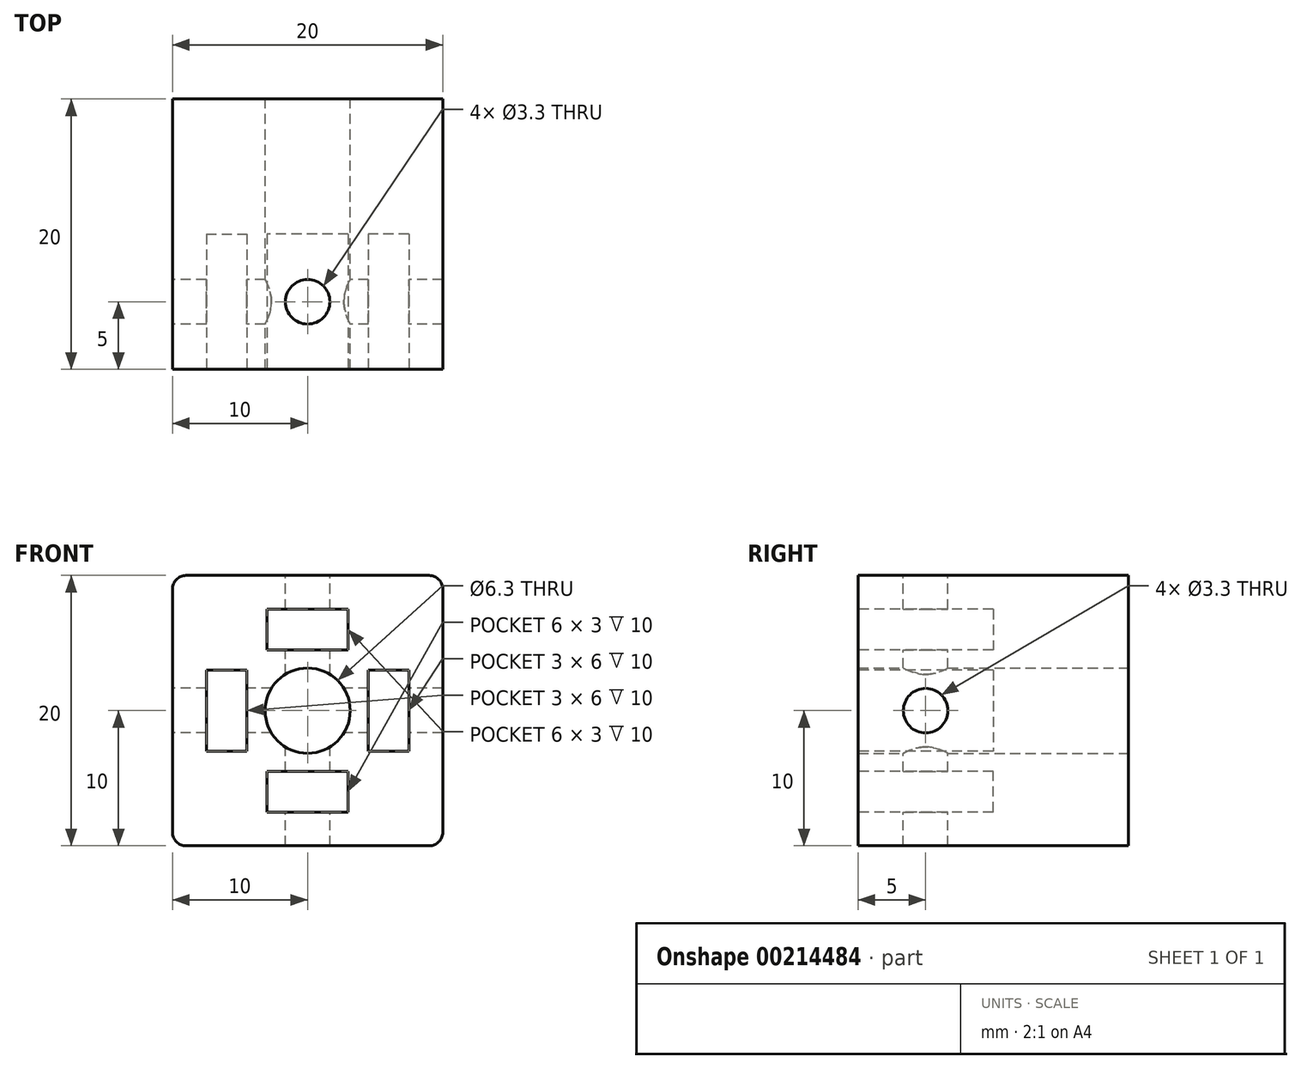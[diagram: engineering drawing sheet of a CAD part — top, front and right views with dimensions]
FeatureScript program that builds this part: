
annotation { "Feature Type Name" : "Feature", "Feature Type Description" : "" }
export const myFeature = defineFeature(function(context is Context, id is Id, definition is map)
    precondition{}
    {
        {
            var Q0;
            Q0=qCreatedBy(makeId("Front.planeOp"),FACE);
            var sketch = newSketch(context, id + "F0", { "sketchPlane" : qUnion([Q0])});
            skLineSegment(sketch, "E0.bottom", {"start": v(10, 10) * mm, "end": v(-10, 10) * mm});
            skLineSegment(sketch, "E0.top", {"start": v(10, -10) * mm, "end": v(-10, -10) * mm});
            skLineSegment(sketch, "E0.left", {"start": v(10, 10) * mm, "end": v(10, -10) * mm});
            skLineSegment(sketch, "E0.right", {"start": v(-10, 10) * mm, "end": v(-10, -10) * mm});
            skPoint(sketch, "E0.middle", {"position": v(0, 0) * mm});
            skCircle(sketch, "E1", {"center": v(0, 0) * mm, "radius": 3.15 * mm});
            skSolve(sketch);
        }
        {
            var Q0;
            Q0 = qSketchRegion(id + "F0", true);
            extrude(context, id + "F1", {"entities" : qUnion([Q0]), "depth" : 20 * mm});
        }
        {
            var Q0;
            Q0=makeQuery(id+"F1.opExtrude","CAP_FACE",FACE,{"disambiguationData":[OSD([sQuery(id+"F0.wireOp",EDGE,"E0.bottom"),sQuery(id+"F0.wireOp",EDGE,"E0.top"),sQuery(id+"F0.wireOp",EDGE,"E0.left"),sQuery(id+"F0.wireOp",EDGE,"E0.right"),sQuery(id+"F0.wireOp",EDGE,"E1")])],"isStart":false});
            var sketch = newSketch(context, id + "F2", { "sketchPlane" : qUnion([Q0])});
            skLineSegment(sketch, "E2", {"start": v(0, 10) * mm, "end": v(0, -10) * mm, "construction": true});
            skLineSegment(sketch, "E3", {"start": v(-10, 0) * mm, "end": v(10, 0) * mm, "construction": true});
            skLineSegment(sketch, "E4.bottom", {"start": v(3, 7.5) * mm, "end": v(-3, 7.5) * mm});
            skLineSegment(sketch, "E4.top", {"start": v(3, 4.5) * mm, "end": v(-3, 4.5) * mm});
            skLineSegment(sketch, "E4.left", {"start": v(3, 7.5) * mm, "end": v(3, 4.5) * mm});
            skLineSegment(sketch, "E4.right", {"start": v(-3, 7.5) * mm, "end": v(-3, 4.5) * mm});
            skPoint(sketch, "E4.middle", {"position": v(0, 6) * mm});
            skLineSegment(sketch, "E5.bottom", {"start": v(-7.5, 3) * mm, "end": v(-4.5, 3) * mm});
            skLineSegment(sketch, "E5.top", {"start": v(-7.5, -3) * mm, "end": v(-4.5, -3) * mm});
            skLineSegment(sketch, "E5.left", {"start": v(-7.5, 3) * mm, "end": v(-7.5, -3) * mm});
            skLineSegment(sketch, "E5.right", {"start": v(-4.5, 3) * mm, "end": v(-4.5, -3) * mm});
            skPoint(sketch, "E5.middle", {"position": v(-6, 0) * mm});
            skLineSegment(sketch, "E6.MirrorCS", {"start": v(3, -4.5) * mm, "end": v(-3, -4.5) * mm});
            skLineSegment(sketch, "E7.MirrorCS", {"start": v(3, -7.5) * mm, "end": v(3, -4.5) * mm});
            skLineSegment(sketch, "E8.MirrorCS", {"start": v(-3, -7.5) * mm, "end": v(-3, -4.5) * mm});
            skLineSegment(sketch, "E9.MirrorCS", {"start": v(3, -7.5) * mm, "end": v(-3, -7.5) * mm});
            skLineSegment(sketch, "E10.MirrorCS", {"start": v(4.5, 3) * mm, "end": v(4.5, -3) * mm});
            skLineSegment(sketch, "E11.MirrorCS", {"start": v(7.5, 3) * mm, "end": v(4.5, 3) * mm});
            skLineSegment(sketch, "E12.MirrorCS", {"start": v(7.5, 3) * mm, "end": v(7.5, -3) * mm});
            skLineSegment(sketch, "E13.MirrorCS", {"start": v(7.5, -3) * mm, "end": v(4.5, -3) * mm});
            skSolve(sketch);
        }
        {
            var Q0;
            Q0=makeQuery(id+"F2.imprint","IMPRINT",FACE,{"disambiguationData":[TD([[makeQuery(id+"F2.imprint","IMPRINT",EDGE,{"derivedFrom":sQuery(id+"F2.wireOp",EDGE,"E4.bottom")}),1.0]])]});
            var Q1;
            Q1=makeQuery(id+"F2.imprint","IMPRINT",FACE,{"disambiguationData":[TD([[makeQuery(id+"F2.imprint","IMPRINT",EDGE,{"derivedFrom":sQuery(id+"F2.wireOp",EDGE,"E5.bottom")}),-1.0]])]});
            var Q2;
            Q2=makeQuery(id+"F2.imprint","IMPRINT",FACE,{"disambiguationData":[TD([[makeQuery(id+"F2.imprint","IMPRINT",EDGE,{"derivedFrom":sQuery(id+"F2.wireOp",EDGE,"E10.MirrorCS")}),1.0]])]});
            var Q3;
            Q3=makeQuery(id+"F2.imprint","IMPRINT",FACE,{"disambiguationData":[TD([[makeQuery(id+"F2.imprint","IMPRINT",EDGE,{"derivedFrom":sQuery(id+"F2.wireOp",EDGE,"E6.MirrorCS")}),1.0]])]});
            extrude(context, id + "F3", {"entities" : qUnion([Q0, Q1, Q2, Q3]), "operationType" : NewBodyOperationType.REMOVE, "oppositeDirection" : true, "depth" : 10 * mm});
        }
        {
            var Q0;
            Q0=makeQuery(id+"F1.opExtrude","SWEPT_FACE",FACE,{"disambiguationData":[OSD([sQuery(id+"F0.wireOp",EDGE,"E0.bottom")])]});
            var sketch = newSketch(context, id + "F4", { "sketchPlane" : qUnion([Q0])});
            skPoint(sketch, "E14", {"position": v(0, -15) * mm});
            skPoint(sketch, "E14.positionSnap0", {"position": v(0, -20) * mm});
            skSolve(sketch);
        }
        {
            var Q0;
            Q0=makeQuery(id+"F1.opExtrude","SWEPT_FACE",FACE,{"disambiguationData":[OSD([sQuery(id+"F0.wireOp",EDGE,"E0.right")])]});
            var sketch = newSketch(context, id + "F5", { "sketchPlane" : qUnion([Q0])});
            skPoint(sketch, "E15", {"position": v(15, 0) * mm});
            skPoint(sketch, "E15.positionSnap0", {"position": v(20, 0) * mm});
            skSolve(sketch);
        }
        {
            var Q0;
            Q0=sQuery(id+"F4.wireOp",VERTEX,"E14");
            var Q1;
            Q1=sQuery(id+"F5.wireOp",VERTEX,"E15");
            var Q2;
            Q2=makeQuery(id+"F1.opExtrude","SWEPT_BODY",BODY,{"disambiguationData":[OSD([sQuery(id+"F0.wireOp",EDGE,"E0.bottom"),sQuery(id+"F0.wireOp",EDGE,"E0.top"),sQuery(id+"F0.wireOp",EDGE,"E0.left"),sQuery(id+"F0.wireOp",EDGE,"E0.right"),sQuery(id+"F0.wireOp",EDGE,"E1")])]});
            hole(context, id + "F6", {"style" : HoleStyle.SIMPLE, "endStyle" : HoleEndStyle.THROUGH, "standardTappedOrClearance" : lookupTablePath({ "standard" : "ISO", "fit" : "Normal", "size" : "M3", "type" : "Clearance" }), "standardBlindInLast" : lookupTablePath({ "fit" : "Standard", "standard" : "ISO", "size" : "M3", "type" : "Clearance" }), "holeDiameter" : 3.3 * mm, "locations" : qUnion([Q0, Q1]), "scope" : qUnion([Q2]), "isTappedThrough" : true});
        }
        {
            var Q0;
            Q0=makeQuery(id+"F1.opExtrude","SWEPT_EDGE",EDGE,{"disambiguationData":[OSD([sQuery(id+"F0.wireOp",EDGE,"E0.bottom"),sQuery(id+"F0.wireOp",EDGE,"E0.right")])]});
            var Q1;
            Q1=makeQuery(id+"F1.opExtrude","SWEPT_EDGE",EDGE,{"disambiguationData":[OSD([sQuery(id+"F0.wireOp",EDGE,"E0.bottom"),sQuery(id+"F0.wireOp",EDGE,"E0.left")])]});
            var Q2;
            Q2=makeQuery(id+"F1.opExtrude","SWEPT_EDGE",EDGE,{"disambiguationData":[OSD([sQuery(id+"F0.wireOp",EDGE,"E0.top"),sQuery(id+"F0.wireOp",EDGE,"E0.right")])]});
            var Q3;
            Q3=makeQuery(id+"F1.opExtrude","SWEPT_EDGE",EDGE,{"disambiguationData":[OSD([sQuery(id+"F0.wireOp",EDGE,"E0.top"),sQuery(id+"F0.wireOp",EDGE,"E0.left")])]});
            fillet(context, id + "F7", {"entities" : qUnion([Q0, Q1, Q2, Q3]), "radius" : 1 * mm, "tangentPropagation" : true, "allowEdgeOverflow" : false});
        }
    });
